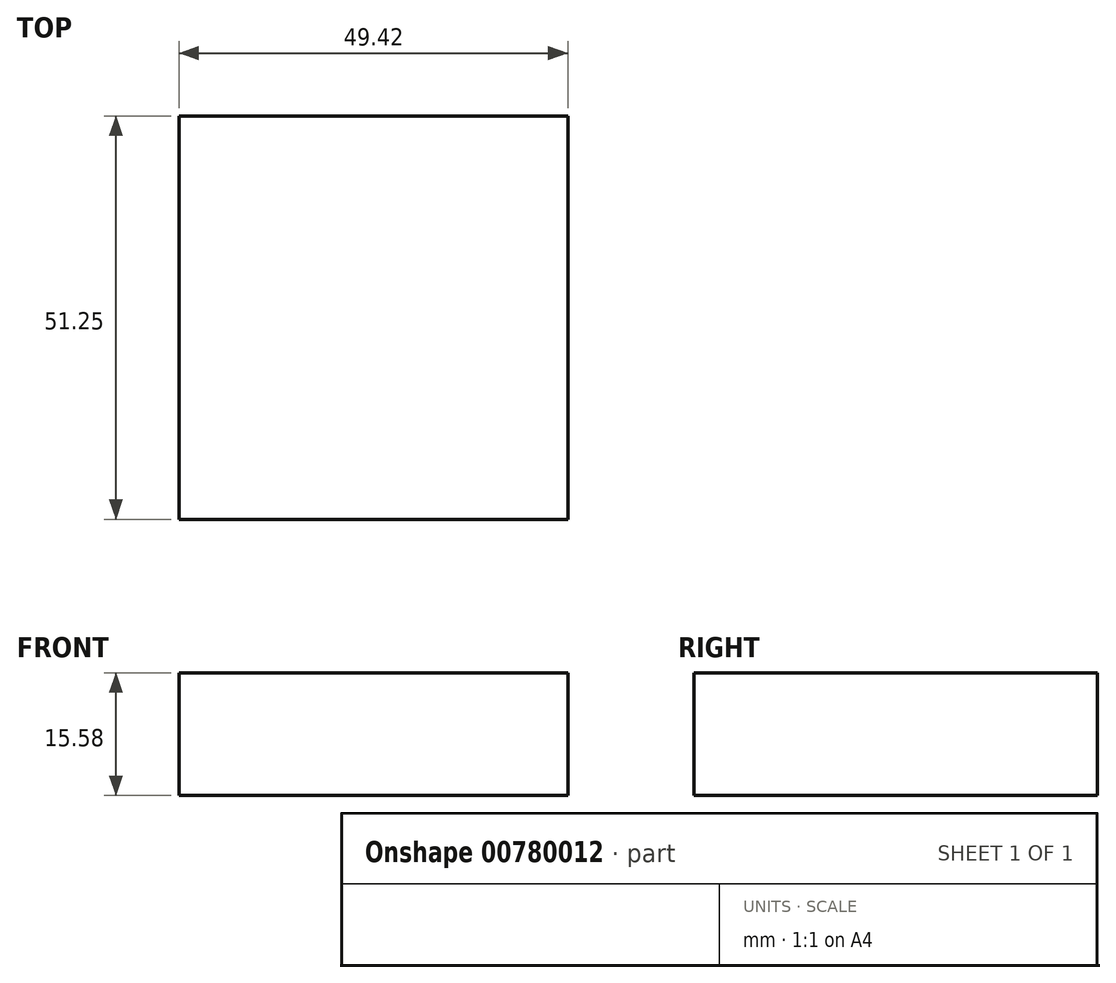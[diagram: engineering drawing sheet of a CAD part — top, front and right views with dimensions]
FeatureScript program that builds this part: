
annotation { "Feature Type Name" : "Feature", "Feature Type Description" : "" }
export const myFeature = defineFeature(function(context is Context, id is Id, definition is map)
    precondition{}
    {
        {
            var Q0;
            Q0=qCreatedBy(makeId("Top.planeOp"),FACE);
            var sketch = newSketch(context, id + "F0", { "sketchPlane" : qUnion([Q0])});
            skLineSegment(sketch, "E0.bottom", {"start": v(7.96, 63.3) * mm, "end": v(57.38, 63.3) * mm});
            skLineSegment(sketch, "E0.top", {"start": v(7.96, 12.05) * mm, "end": v(57.38, 12.05) * mm});
            skLineSegment(sketch, "E0.left", {"start": v(7.96, 63.3) * mm, "end": v(7.96, 12.05) * mm});
            skLineSegment(sketch, "E0.right", {"start": v(57.38, 63.3) * mm, "end": v(57.38, 12.05) * mm});
            skSolve(sketch);
        }
        {
            var Q0;
            Q0=makeQuery(id+"F0.imprint","IMPRINT",FACE,{"disambiguationData":[TD([[makeQuery(id+"F0.imprint","IMPRINT",EDGE,{"derivedFrom":sQuery(id+"F0.wireOp",EDGE,"E0.bottom")}),-1.0]])]});
            extrude(context, id + "F1", {"entities" : qUnion([Q0]), "oppositeDirection" : true, "depth" : 15.58 * mm, "offsetDistance" : 25 * mm});
        }
    });
